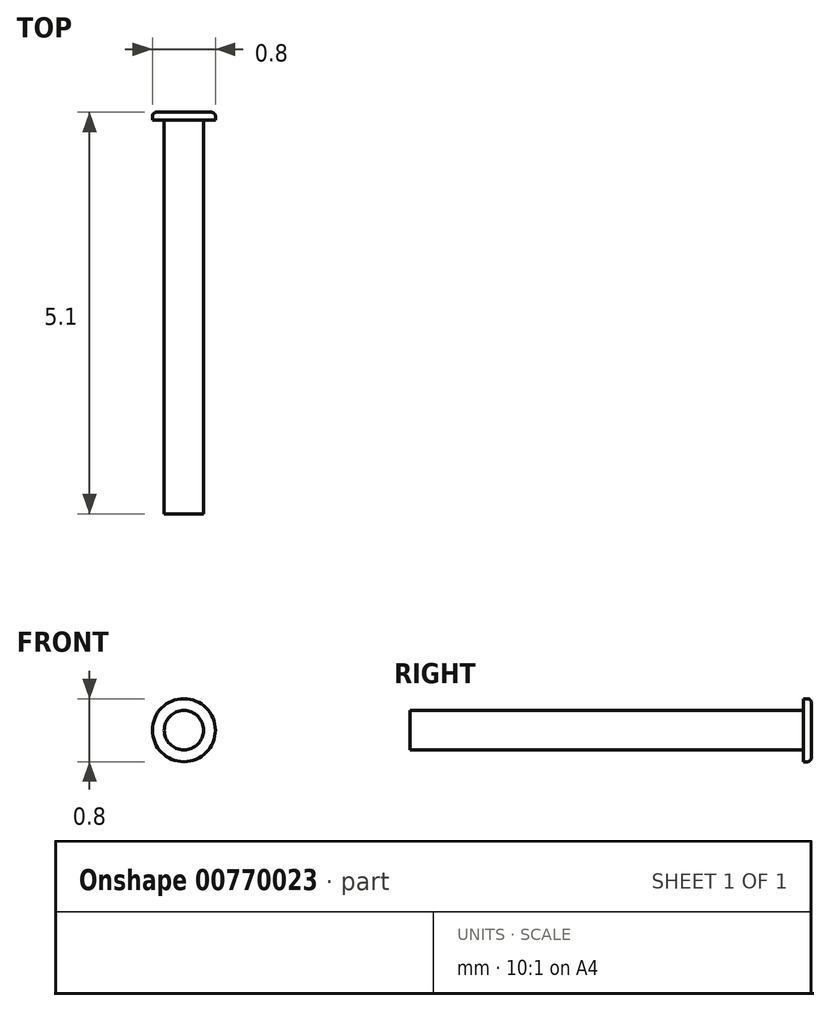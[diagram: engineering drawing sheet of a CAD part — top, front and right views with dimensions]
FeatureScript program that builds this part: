
annotation { "Feature Type Name" : "Feature", "Feature Type Description" : "" }
export const myFeature = defineFeature(function(context is Context, id is Id, definition is map)
    precondition{}
    {
        {
            var Q0;
            Q0=qCreatedBy(makeId("Front.planeOp"),FACE);
            var sketch = newSketch(context, id + "F0", { "sketchPlane" : qUnion([Q0])});
            skCircle(sketch, "E0", {"center": v(0, 0) * mm, "radius": 0.4 * mm});
            skSolve(sketch);
        }
        {
            var Q0;
            Q0 = qSketchRegion(id + "F0", true);
            extrude(context, id + "F1", {"entities" : qUnion([Q0]), "oppositeDirection" : true, "depth" : 0.1 * mm, "offsetDistance" : 25 * mm});
        }
        {
            var Q0;
            Q0=makeQuery(id+"F1.opExtrude","CAP_EDGE",EDGE,{"disambiguationData":[OSD([sQuery(id+"F0.wireOp",EDGE,"E0")])],"isStart":false});
            fillet(context, id + "F2", {"entities" : qUnion([Q0]), "radius" : 0.05 * mm, "tangentPropagation" : true, "allowEdgeOverflow" : false});
        }
        {
            var Q0;
            Q0=makeQuery(id+"F1.opExtrude","CAP_FACE",FACE,{"disambiguationData":[OSD([sQuery(id+"F0.wireOp",EDGE,"E0")])],"isStart":true});
            var sketch = newSketch(context, id + "F3", { "sketchPlane" : qUnion([Q0])});
            skCircle(sketch, "E1", {"center": v(0, 0) * mm, "radius": 0.25 * mm});
            skSolve(sketch);
        }
        {
            var Q0;
            Q0 = qSketchRegion(id + "F3", true);
            extrude(context, id + "F4", {"entities" : qUnion([Q0]), "operationType" : NewBodyOperationType.ADD, "depth" : 5 * mm, "offsetDistance" : 25 * mm});
        }
    });
